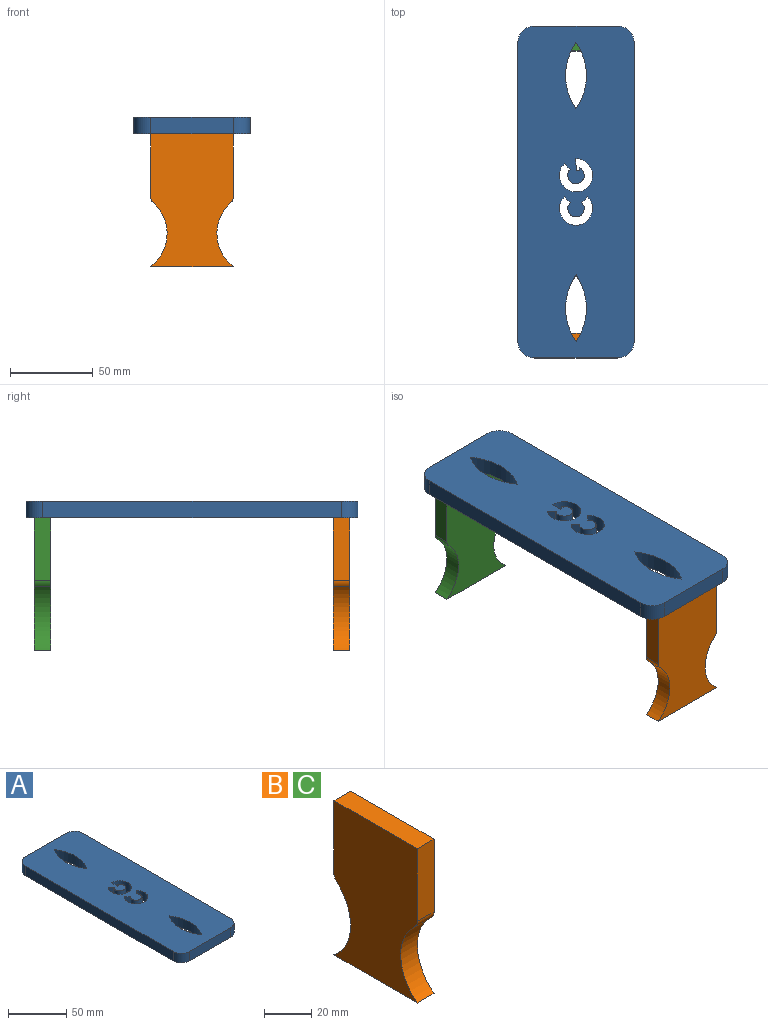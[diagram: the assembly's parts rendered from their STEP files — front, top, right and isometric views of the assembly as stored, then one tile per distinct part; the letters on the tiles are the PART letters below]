
ASSEMBLY  parts=3 mates=2
PART A: 24 faces, bbox 70x200x10 mm
  f0: plane 200x70mm, normal (0,0,1), area 12843.1mm2, adj f2,f3,f4,f5,f6,f7,f8,f9
  f1: plane 200x70mm, normal (0,0,-1), area 12843.1mm2, adj f2,f3,f4,f5,f6,f7,f8,f9
  f2: plane 50x10mm, normal (0,1,0), area 500mm2, adj f0,f1,f21,f23
  f3: plane 180x10mm, normal (-1,0,0), area 1800mm2, adj f0,f1,f21,f22
  f4: plane 50x10mm, normal (0,-1,0), area 500mm2, adj f0,f1,f20,f22
  f5: plane 180x10mm, normal (1,0,0), area 1800mm2, adj f0,f1,f20,f23
  f6: cylinder r=5mm len=10mm, axis (0,0,1), area 255.6mm2, adj f0,f1,f7,f11
  f7: plane 10x3.54mm, normal (-0.71,-0.71,0), area 50mm2, adj f0,f1,f6,f8
  f8: cylinder r=10mm len=20mm, axis (0,0,1), area 551mm2, adj f0,f1,f7,f9
  f9: plane 10x7mm, normal (1,0,0), area 70mm2, adj f0,f1,f8,f10
  f10: plane 10x2mm, normal (0,1,0), area 20mm2, adj f0,f1,f9,f11
  f11: plane 10x1.58mm, normal (-1,0,0), area 15.8mm2, adj f0,f1,f6,f10
  f12: cylinder r=5mm len=10mm, axis (0,0,1), area 238.2mm2, adj f0,f1,f13,f15
  f13: plane 10x3.54mm, normal (-0.71,-0.71,0), area 50mm2, adj f0,f1,f12,f14
  f14: cylinder r=10mm len=20mm, axis (0,0,1), area 473.6mm2, adj f0,f1,f13,f15
  f15: plane 10x3.54mm, normal (0.71,-0.71,0), area 50mm2, adj f0,f1,f12,f14
  f16: cylinder r=35mm len=40mm, axis (0,0,1), area 425.8mm2, adj f0,f1,f17
  f17: cylinder r=35mm len=40mm, axis (0,0,1), area 425.8mm2, adj f0,f1,f16
  f18: cylinder r=35mm len=40mm, axis (0,0,1), area 425.8mm2, adj f0,f1,f19
  f19: cylinder r=35mm len=40mm, axis (0,0,1), area 425.8mm2, adj f0,f1,f18
  f20: cylinder r=10mm len=10mm, axis (0,0,-1), area 157.1mm2, adj f0,f1,f4,f5
  f21: cylinder r=10mm len=10mm, axis (0,0,1), area 157.1mm2, adj f0,f1,f2,f3
  f22: cylinder r=10mm len=10mm, axis (0,0,-1), area 157.1mm2, adj f0,f1,f3,f4
  f23: cylinder r=10mm len=10mm, axis (0,0,1), area 157.1mm2, adj f0,f1,f2,f5
PART B: 10 faces, bbox 10x50x80 mm
  f0: cylinder r=25mm len=38.63mm, axis (-1,0,0), area 442.1mm2, adj f1,f7,f8,f9
  f1: cylinder r=5mm len=10mm, axis (-1,0,0), area 42.1mm2, adj f0,f2,f8,f9
  f2: plane 37.64x10mm, normal (0,1,0), area 376.4mm2, adj f1,f3,f8,f9
  f3: plane 50x10mm, normal (0,0,1), area 500mm2, adj f2,f4,f8,f9
  f4: plane 37.64x10mm, normal (0,-1,0), area 376.4mm2, adj f3,f5,f8,f9
  f5: cylinder r=5mm len=10mm, axis (-1,0,0), area 42.1mm2, adj f4,f6,f8,f9
  f6: cylinder r=25mm len=38.63mm, axis (-1,0,0), area 442.1mm2, adj f5,f7,f8,f9
  f7: plane 50x10mm, normal (0,0,-1), area 500mm2, adj f0,f6,f8,f9
  f8: plane 80x50mm, normal (1,0,0), area 3439.4mm2, adj f0,f1,f2,f3,f4,f5,f6,f7
  f9: plane 80x50mm, normal (-1,0,0), area 3439.4mm2, adj f0,f1,f2,f3,f4,f5,f6,f7
PART C: same geometry as B
PLACE A t=(-61.4,-0.81,-10.67)mm
PLACE B rot(axis=(0,0,1),90deg) t=(-28.81,-56.29,-71.28)mm
PLACE C rot(axis=(0,0,1),90deg) t=(-28.81,123.71,-71.28)mm
MATE fastened B.f3 <-> A.f1  axis (0,0,1) through (-48.04,-51.29,-10.67)mm
MATE fastened C.f3 <-> A.f1  axis (0,0,1) through (-48.04,128.71,-10.67)mm
